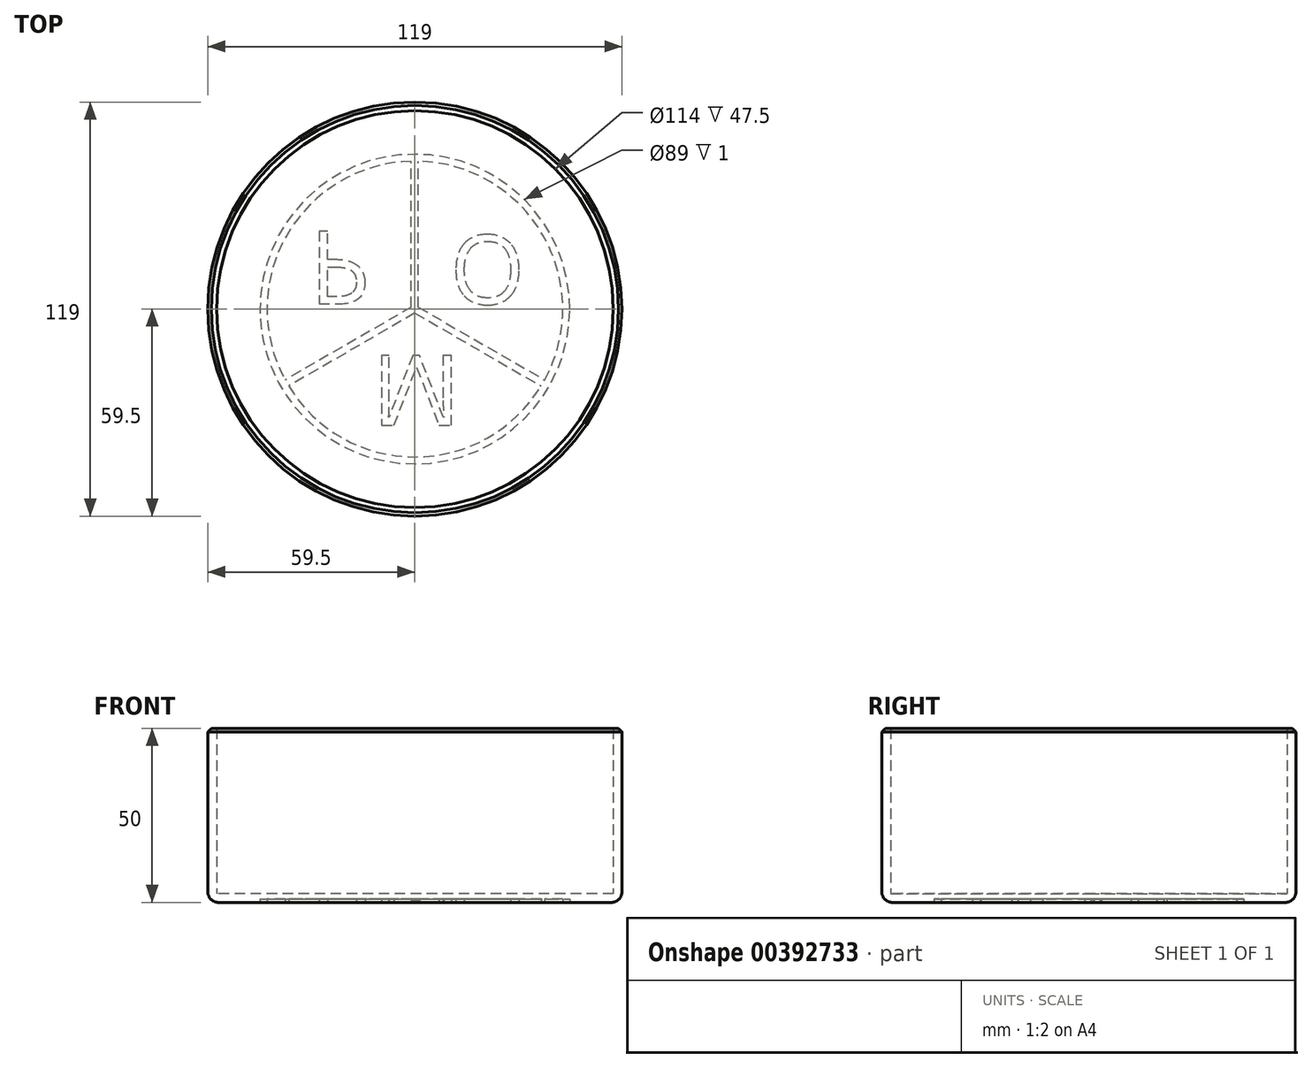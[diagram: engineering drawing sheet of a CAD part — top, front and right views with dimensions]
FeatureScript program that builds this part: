
annotation { "Feature Type Name" : "Feature", "Feature Type Description" : "" }
export const myFeature = defineFeature(function(context is Context, id is Id, definition is map)
    precondition{}
    {
        {
            var Q0;
            Q0=qCreatedBy(makeId("Top.planeOp"),FACE);
            var sketch = newSketch(context, id + "F0", { "sketchPlane" : qUnion([Q0])});
            skCircle(sketch, "E0", {"center": v(0, 0) * mm, "radius": 59.5 * mm});
            skSolve(sketch);
        }
        {
            var Q0;
            Q0=makeQuery(id+"F0.imprint","IMPRINT",FACE,{"disambiguationData":[TD([[makeQuery(id+"F0.imprint","IMPRINT",EDGE,{"derivedFrom":sQuery(id+"F0.wireOp",EDGE,"E0")}),1.0]])]});
            extrude(context, id + "F1", {"entities" : qUnion([Q0]), "depth" : 50 * mm});
        }
        {
            var Q0;
            Q0=makeQuery(id+"F1.opExtrude","CAP_FACE",FACE,{"disambiguationData":[OSD([sQuery(id+"F0.wireOp",EDGE,"E0")])],"isStart":false});
            shell(context, id + "F2", {"entities" : qUnion([Q0]), "thickness" : 2.5 * mm});
        }
        {
            var Q0;
            Q0=makeQuery(id+"F1.opExtrude","CAP_EDGE",EDGE,{"disambiguationData":[OSD([sQuery(id+"F0.wireOp",EDGE,"E0")])],"isStart":true});
            fillet(context, id + "F3", {"entities" : qUnion([Q0]), "radius" : 3 * mm, "tangentPropagation" : true, "allowEdgeOverflow" : false});
        }
        {
            var Q0;
            Q0=makeQuery(id+"F1.opExtrude","CAP_FACE",FACE,{"disambiguationData":[OSD([sQuery(id+"F0.wireOp",EDGE,"E0")])],"isStart":true});
            var sketch = newSketch(context, id + "F4", { "sketchPlane" : qUnion([Q0])});
            skCircle(sketch, "E1", {"center": v(0, 0) * mm, "radius": 42.5 * mm});
            skPoint(sketch, "E2.secondSnap0", {"position": v(18.4, 10.62) * mm});
            skText(sketch, "E3", { "text": "M", "fontName": "OpenSans-Regular.ttf"});
            skText(sketch, "E4", { "text": "P", "fontName": "OpenSans-Regular.ttf"});
            skText(sketch, "E5", { "text": "O", "fontName": "OpenSans-Regular.ttf"});
            skLineSegment(sketch, "E6.left", {"start": v(-1, -0.58) * mm, "end": v(-1, -42.49) * mm});
            skLineSegment(sketch, "E6.right", {"start": v(1, -0.58) * mm, "end": v(1, -42.49) * mm});
            skLineSegment(sketch, "E7.1.0", {"start": v(0, 1.15) * mm, "end": v(36.3, 22.11) * mm});
            skLineSegment(sketch, "E7.1.1", {"start": v(1, -0.58) * mm, "end": v(37.3, 20.38) * mm});
            skLineSegment(sketch, "E7.2.0", {"start": v(-1, -0.58) * mm, "end": v(-37.3, 20.38) * mm});
            skLineSegment(sketch, "E7.2.1", {"start": v(0, 1.15) * mm, "end": v(-36.3, 22.11) * mm});
            skCircle(sketch, "E8", {"center": v(0, 0) * mm, "radius": 44.5 * mm});
            skPoint(sketch, "E9.orphan", {"position": v(0.5, 0.87) * mm});
            skPoint(sketch, "E10.orphan", {"position": v(-0.5, 0.87) * mm});
            skPoint(sketch, "E11.orphan", {"position": v(-1, 0) * mm});
            skPoint(sketch, "E12.orphan", {"position": v(1, 0) * mm});
            skPoint(sketch, "E13.orphan", {"position": v(0.5, -0.87) * mm});
            skPoint(sketch, "E14.orphan", {"position": v(-0.5, -0.87) * mm});
            const initialGuessF4  = {"E3": [-0.01229, 0.01326, 1, 0, 0.02034], "E4": [-0.0304, -0.0224, 1, 0, 0.02108], "E5": [0.0101, -0.02121, 1, 0, 0.0199]};
            skSetInitialGuess(sketch, initialGuessF4);
            skSolve(sketch);
        }
        {
            var Q0;
            Q0=makeQuery(id+"F4.imprint","IMPRINT",FACE,{"disambiguationData":[TD([[makeQuery(id+"F4.imprint","IMPRINT",EDGE,{"derivedFrom":sQuery(id+"F4.wireOp",EDGE,"E8")}),1.0]])]});
            var Q1;
            {var subQ0=sQuery(id+"F4.wireOp",EDGE,"E6.left");Q1=makeQuery(id+"F4.imprint","IMPRINT",FACE,{"disambiguationData":[TD([[makeQuery(id+"F4.imprint","IMPRINT",EDGE,{"derivedFrom":subQ0}),1.0]])]});}
            var Q2;
            Q2=makeQuery(id+"F4.imprint","IMPRINT",FACE,{"disambiguationData":[TD([[makeQuery(id+"F4.imprint","IMPRINT",EDGE,{"derivedFrom":sQuery(id+"F4.wireOp",EDGE,"E4.sketch_text.stroke-0")}),-1.0]])]});
            var Q3;
            Q3=makeQuery(id+"F4.imprint","IMPRINT",FACE,{"disambiguationData":[TD([[makeQuery(id+"F4.imprint","IMPRINT",EDGE,{"derivedFrom":sQuery(id+"F4.wireOp",EDGE,"E3.sketch_text.stroke-0")}),-1.0]])]});
            var Q4;
            Q4=makeQuery(id+"F4.imprint","IMPRINT",FACE,{"disambiguationData":[TD([[makeQuery(id+"F4.imprint","IMPRINT",EDGE,{"derivedFrom":sQuery(id+"F4.wireOp",EDGE,"E5.sketch_text.stroke-0")}),-1.0]])]});
            extrude(context, id + "F5", {"entities" : qUnion([Q0, Q1, Q2, Q3, Q4]), "operationType" : NewBodyOperationType.REMOVE, "oppositeDirection" : true, "depth" : 1 * mm});
        }
        {
            var Q0;
            Q0=makeQuery(id+"F1.opExtrude","CAP_EDGE",EDGE,{"disambiguationData":[OSD([sQuery(id+"F0.wireOp",EDGE,"E0")])],"isStart":false});
            chamfer(context, id + "F6", {"entities" : qUnion([Q0]), "width" : 1 * mm, "tangentPropagation" : true});
        }
    });
